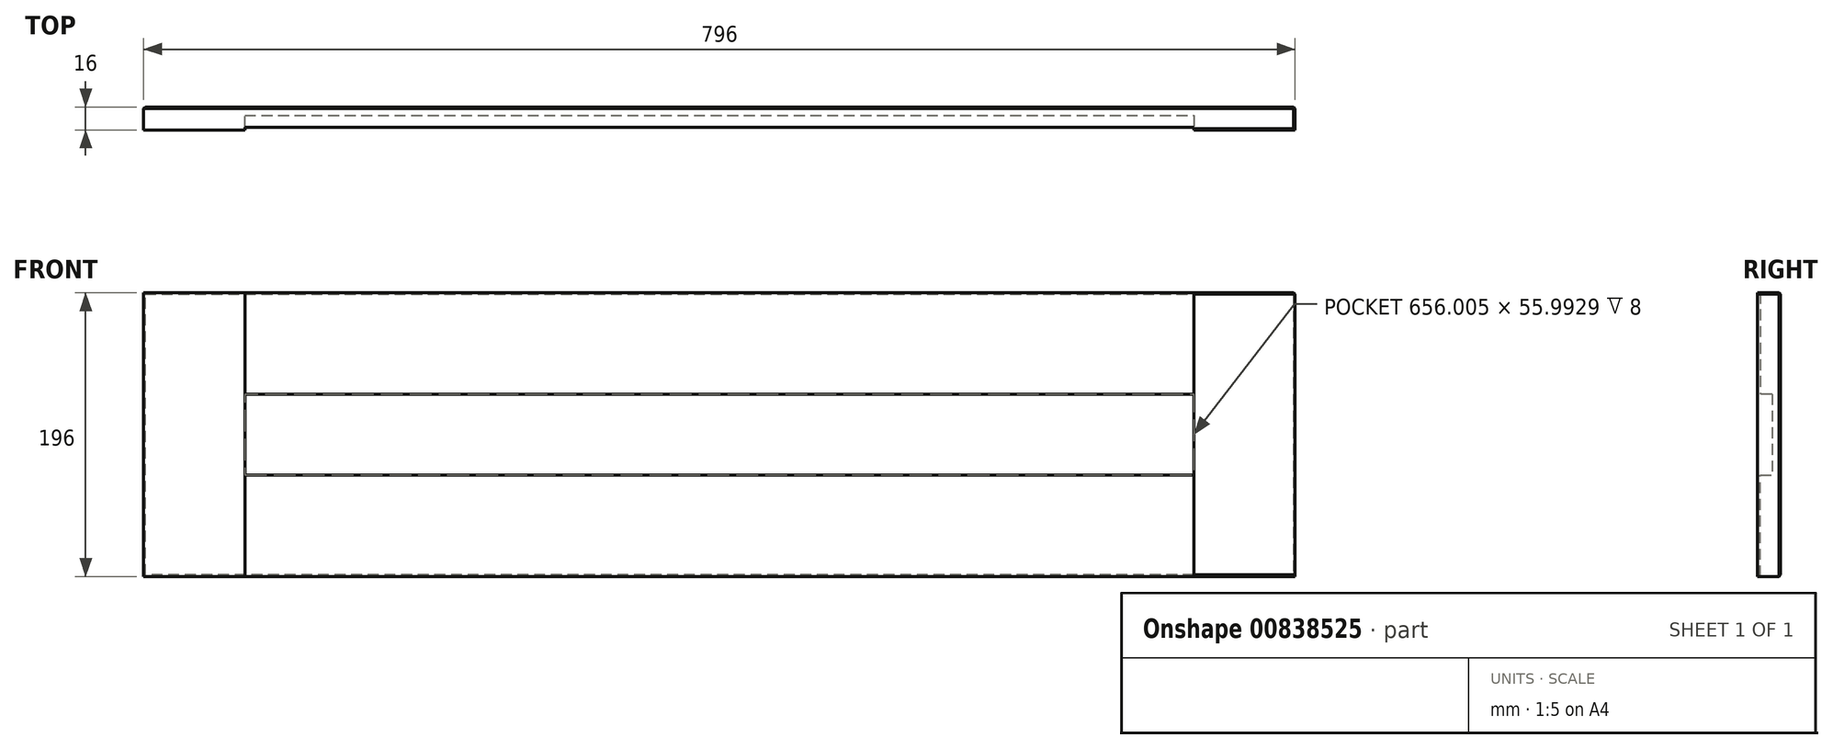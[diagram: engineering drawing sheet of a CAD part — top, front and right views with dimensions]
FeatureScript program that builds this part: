
annotation { "Feature Type Name" : "Feature", "Feature Type Description" : "" }
export const myFeature = defineFeature(function(context is Context, id is Id, definition is map)
    precondition{}
    {
        {
            var Q0;
            Q0=qCreatedBy(makeId("Front.planeOp"),FACE);
            var sketch = newSketch(context, id + "F0", { "sketchPlane" : qUnion([Q0])});
            skLineSegment(sketch, "E0.bottom", {"start": v(0, 0) * mm, "end": v(35.9, 0) * mm});
            skLineSegment(sketch, "E0.top", {"start": v(0, 30.12) * mm, "end": v(35.9, 30.12) * mm});
            skLineSegment(sketch, "E0.left", {"start": v(0, 0) * mm, "end": v(0, 30.12) * mm});
            skLineSegment(sketch, "E0.right", {"start": v(35.9, 0) * mm, "end": v(35.9, 30.12) * mm});
            skSolve(sketch);
        }
        {
            var Q0;
            Q0=makeQuery(id+"F0.imprint","IMPRINT",FACE,{"disambiguationData":[TD([[makeQuery(id+"F0.imprint","IMPRINT",EDGE,{"derivedFrom":sQuery(id+"F0.wireOp",EDGE,"E0.bottom")}),1.0]])]});
            extrude(context, id + "F1", {"entities" : qUnion([Q0]), "depth" : 16 * mm, "offsetDistance" : 25.4 * mm});
        }
        {
            var Q0;
            Q0=makeQuery(id+"F1.opExtrude","SWEPT_FACE",FACE,{"disambiguationData":[OSD([sQuery(id+"F0.wireOp",EDGE,"E0.left")])]});
            extrude(context, id + "F2", {"entities" : qUnion([Q0]), "operationType" : NewBodyOperationType.ADD, "oppositeDirection" : true, "depth" : 196 * mm, "offsetDistance" : 25 * mm});
        }
        {
            var Q0;
            {var subQ0=sQuery(id+"F0.wireOp",EDGE,"E0.bottom");Q0=makeQuery(id+"F2.boolean.opBoolean","MERGE",FACE,{"derivedFrom":[makeQuery(id+"F1.opExtrude","SWEPT_FACE",FACE,{"disambiguationData":[OSD([subQ0])]}),makeQuery(id+"F2.opExtrude","SWEPT_FACE",FACE,{"disambiguationData":[OSD([subQ0,sQuery(id+"F0.wireOp",EDGE,"E0.left")])]})]});}
            extrude(context, id + "F3", {"entities" : qUnion([Q0]), "operationType" : NewBodyOperationType.ADD, "oppositeDirection" : true, "depth" : 796 * mm, "offsetDistance" : 25 * mm});
        }
        {
            var Q0;
            {var subQ0=sQuery(id+"F0.wireOp",EDGE,"E0.left");var subQ1=sQuery(id+"F0.wireOp",EDGE,"E0.bottom");Q0=makeQuery(id+"F3.boolean.opBoolean","MERGE",FACE,{"derivedFrom":[makeQuery(id+"F2.boolean.opBoolean","MERGE",FACE,{"derivedFrom":[makeQuery(id+"F1.opExtrude","CAP_FACE",FACE,{"disambiguationData":[OSD([subQ1,sQuery(id+"F0.wireOp",EDGE,"E0.top"),subQ0,sQuery(id+"F0.wireOp",EDGE,"E0.right")])],"isStart":false}),makeQuery(id+"F2.opExtrude","SWEPT_FACE",FACE,{"disambiguationData":[OSD([subQ0]),TDD([makeQuery(id+"F1.opExtrude","CAP_EDGE",EDGE,{"disambiguationData":[OSD([subQ0])],"isStart":false})])]})]}),makeQuery(id+"F3.opExtrude","SWEPT_FACE",FACE,{"disambiguationData":[OSD([subQ1,subQ0]),TDD([makeQuery(id+"F2.boolean.opBoolean","MERGE",EDGE,{"derivedFrom":[makeQuery(id+"F1.opExtrude","CAP_EDGE",EDGE,{"disambiguationData":[OSD([subQ1])],"isStart":false}),makeQuery(id+"F2.opExtrude","SWEPT_EDGE",EDGE,{"disambiguationData":[OSD([subQ1,subQ0]),TDD([makeQuery(id+"F1.opExtrude","CAP_VERTEX",VERTEX,{"disambiguationData":[OSD([subQ1,subQ0])],"isStart":false})])]})]})])]})]});}
            var sketch = newSketch(context, id + "F4", { "sketchPlane" : qUnion([Q0])});
            skLineSegment(sketch, "E1.bottom", {"start": v(0, 796) * mm, "end": v(42.19, 796) * mm});
            skLineSegment(sketch, "E1.top", {"start": v(0, 751.57) * mm, "end": v(42.19, 751.57) * mm});
            skLineSegment(sketch, "E1.left", {"start": v(0, 796) * mm, "end": v(0, 751.57) * mm});
            skLineSegment(sketch, "E1.right", {"start": v(42.19, 796) * mm, "end": v(42.19, 751.57) * mm});
            skLineSegment(sketch, "E2.bottom", {"start": v(196, 796) * mm, "end": v(153.6, 796) * mm});
            skLineSegment(sketch, "E2.top", {"start": v(196, 746.75) * mm, "end": v(153.6, 746.75) * mm});
            skLineSegment(sketch, "E2.left", {"start": v(196, 796) * mm, "end": v(196, 746.75) * mm});
            skLineSegment(sketch, "E2.right", {"start": v(153.6, 796) * mm, "end": v(153.6, 746.75) * mm});
            skSolve(sketch);
        }
        {
            var Q0;
            Q0=makeQuery(id+"F4.imprint","IMPRINT",FACE,{"disambiguationData":[TD([[makeQuery(id+"F4.imprint","IMPRINT",EDGE,{"derivedFrom":sQuery(id+"F4.wireOp",EDGE,"E1.bottom")}),-1.0]])]});
            var Q1;
            Q1=makeQuery(id+"F4.imprint","IMPRINT",FACE,{"disambiguationData":[TD([[makeQuery(id+"F4.imprint","IMPRINT",EDGE,{"derivedFrom":sQuery(id+"F4.wireOp",EDGE,"E2.bottom")}),-1.0]])]});
            extrude(context, id + "F5", {"entities" : qUnion([Q0, Q1]), "operationType" : NewBodyOperationType.ADD, "depth" : 25 * mm, "offsetDistance" : 25 * mm});
        }
        {
            var Q0;
            {var subQ0=sQuery(id+"F0.wireOp",EDGE,"E0.left");var subQ1=sQuery(id+"F0.wireOp",EDGE,"E0.bottom");Q0=makeQuery(id+"F3.boolean.opBoolean","MERGE",FACE,{"derivedFrom":[makeQuery(id+"F2.boolean.opBoolean","MERGE",FACE,{"derivedFrom":[makeQuery(id+"F1.opExtrude","CAP_FACE",FACE,{"disambiguationData":[OSD([subQ1,sQuery(id+"F0.wireOp",EDGE,"E0.top"),subQ0,sQuery(id+"F0.wireOp",EDGE,"E0.right")])],"isStart":false}),makeQuery(id+"F2.opExtrude","SWEPT_FACE",FACE,{"disambiguationData":[OSD([subQ0]),TDD([makeQuery(id+"F1.opExtrude","CAP_EDGE",EDGE,{"disambiguationData":[OSD([subQ0])],"isStart":false})])]})]}),makeQuery(id+"F3.opExtrude","SWEPT_FACE",FACE,{"disambiguationData":[OSD([subQ1,subQ0]),TDD([makeQuery(id+"F2.boolean.opBoolean","MERGE",EDGE,{"derivedFrom":[makeQuery(id+"F1.opExtrude","CAP_EDGE",EDGE,{"disambiguationData":[OSD([subQ1])],"isStart":false}),makeQuery(id+"F2.opExtrude","SWEPT_EDGE",EDGE,{"disambiguationData":[OSD([subQ1,subQ0]),TDD([makeQuery(id+"F1.opExtrude","CAP_VERTEX",VERTEX,{"disambiguationData":[OSD([subQ1,subQ0])],"isStart":false})])]})]})])]})]});}
            var sketch = newSketch(context, id + "F6", { "sketchPlane" : qUnion([Q0])});
            skLineSegment(sketch, "E3.bottom", {"start": v(196, 0) * mm, "end": v(163.38, 0) * mm});
            skLineSegment(sketch, "E3.top", {"start": v(196, 46.55) * mm, "end": v(163.38, 46.55) * mm});
            skLineSegment(sketch, "E3.left", {"start": v(196, 0) * mm, "end": v(196, 46.55) * mm});
            skLineSegment(sketch, "E3.right", {"start": v(163.38, 0) * mm, "end": v(163.38, 46.55) * mm});
            skLineSegment(sketch, "E4.bottom", {"start": v(0, 0) * mm, "end": v(50.28, 0) * mm});
            skLineSegment(sketch, "E4.top", {"start": v(0, 44.4) * mm, "end": v(50.28, 44.4) * mm});
            skLineSegment(sketch, "E4.left", {"start": v(0, 0) * mm, "end": v(0, 44.4) * mm});
            skLineSegment(sketch, "E4.right", {"start": v(50.28, 0) * mm, "end": v(50.28, 44.4) * mm});
            skSolve(sketch);
        }
        {
            var Q0;
            Q0=makeQuery(id+"F6.imprint","IMPRINT",FACE,{"disambiguationData":[TD([[makeQuery(id+"F6.imprint","IMPRINT",EDGE,{"derivedFrom":sQuery(id+"F6.wireOp",EDGE,"E3.bottom")}),1.0]])]});
            var Q1;
            Q1=makeQuery(id+"F6.imprint","IMPRINT",FACE,{"disambiguationData":[TD([[makeQuery(id+"F6.imprint","IMPRINT",EDGE,{"derivedFrom":sQuery(id+"F6.wireOp",EDGE,"E4.bottom")}),1.0]])]});
            extrude(context, id + "F7", {"entities" : qUnion([Q0, Q1]), "operationType" : NewBodyOperationType.ADD, "depth" : 25 * mm, "offsetDistance" : 25 * mm});
        }
        {
            var Q0;
            Q0=makeQuery(id+"F7.opExtrude","SWEPT_FACE",FACE,{"disambiguationData":[OSD([sQuery(id+"F6.wireOp",EDGE,"E4.right")])]});
            extrude(context, id + "F8", {"entities" : qUnion([Q0]), "operationType" : NewBodyOperationType.ADD, "depth" : 19.72 * mm, "offsetDistance" : 25 * mm});
        }
        {
            var Q0;
            {var subQ0=sQuery(id+"F6.wireOp",EDGE,"E4.top");Q0=makeQuery(id+"F8.boolean.opBoolean","MERGE",FACE,{"derivedFrom":[makeQuery(id+"F7.opExtrude","SWEPT_FACE",FACE,{"disambiguationData":[OSD([subQ0])]}),makeQuery(id+"F8.opExtrude","SWEPT_FACE",FACE,{"disambiguationData":[OSD([subQ0,sQuery(id+"F6.wireOp",EDGE,"E4.right")])]})]});}
            extrude(context, id + "F9", {"entities" : qUnion([Q0]), "operationType" : NewBodyOperationType.ADD, "depth" : 25.6 * mm, "offsetDistance" : 25 * mm});
        }
        {
            var Q0;
            Q0=makeQuery(id+"F7.opExtrude","SWEPT_FACE",FACE,{"disambiguationData":[OSD([sQuery(id+"F6.wireOp",EDGE,"E3.right")])]});
            extrude(context, id + "F10", {"entities" : qUnion([Q0]), "operationType" : NewBodyOperationType.ADD, "depth" : 37.38 * mm, "offsetDistance" : 25 * mm});
        }
        {
            var Q0;
            {var subQ0=sQuery(id+"F6.wireOp",EDGE,"E3.top");Q0=makeQuery(id+"F10.boolean.opBoolean","MERGE",FACE,{"derivedFrom":[makeQuery(id+"F7.opExtrude","SWEPT_FACE",FACE,{"disambiguationData":[OSD([subQ0])]}),makeQuery(id+"F10.opExtrude","SWEPT_FACE",FACE,{"disambiguationData":[OSD([subQ0,sQuery(id+"F6.wireOp",EDGE,"E3.right")])]})]});}
            extrude(context, id + "F11", {"entities" : qUnion([Q0]), "operationType" : NewBodyOperationType.ADD, "depth" : 23.45 * mm, "offsetDistance" : 25 * mm});
        }
        {
            var Q0;
            Q0=makeQuery(id+"F5.opExtrude","SWEPT_FACE",FACE,{"disambiguationData":[OSD([sQuery(id+"F4.wireOp",EDGE,"E1.right")])]});
            extrude(context, id + "F12", {"entities" : qUnion([Q0]), "operationType" : NewBodyOperationType.ADD, "depth" : 27.8 * mm, "offsetDistance" : 25 * mm});
        }
        {
            var Q0;
            {var subQ0=sQuery(id+"F4.wireOp",EDGE,"E1.top");Q0=makeQuery(id+"F12.boolean.opBoolean","MERGE",FACE,{"derivedFrom":[makeQuery(id+"F5.opExtrude","SWEPT_FACE",FACE,{"disambiguationData":[OSD([subQ0])]}),makeQuery(id+"F12.opExtrude","SWEPT_FACE",FACE,{"disambiguationData":[OSD([subQ0,sQuery(id+"F4.wireOp",EDGE,"E1.right")])]})]});}
            extrude(context, id + "F13", {"entities" : qUnion([Q0]), "operationType" : NewBodyOperationType.ADD, "depth" : 25.57 * mm, "offsetDistance" : 25 * mm});
        }
        {
            var Q0;
            Q0=makeQuery(id+"F5.opExtrude","SWEPT_FACE",FACE,{"disambiguationData":[OSD([sQuery(id+"F4.wireOp",EDGE,"E2.top")])]});
            extrude(context, id + "F14", {"entities" : qUnion([Q0]), "operationType" : NewBodyOperationType.ADD, "depth" : 20.75 * mm, "offsetDistance" : 25 * mm});
        }
        {
            var Q0;
            {var subQ0=sQuery(id+"F4.wireOp",EDGE,"E2.right");Q0=makeQuery(id+"F14.boolean.opBoolean","MERGE",FACE,{"derivedFrom":[makeQuery(id+"F5.opExtrude","SWEPT_FACE",FACE,{"disambiguationData":[OSD([subQ0])]}),makeQuery(id+"F14.opExtrude","SWEPT_FACE",FACE,{"disambiguationData":[OSD([sQuery(id+"F4.wireOp",EDGE,"E2.top"),subQ0])]})]});}
            extrude(context, id + "F15", {"entities" : qUnion([Q0]), "operationType" : NewBodyOperationType.ADD, "depth" : 27.6 * mm, "offsetDistance" : 25 * mm});
        }
        {
            var Q0;
            {var subQ0=sQuery(id+"F0.wireOp",EDGE,"E0.left");var subQ1=sQuery(id+"F0.wireOp",EDGE,"E0.bottom");Q0=makeQuery(id+"F3.boolean.opBoolean","MERGE",FACE,{"derivedFrom":[makeQuery(id+"F2.boolean.opBoolean","MERGE",FACE,{"derivedFrom":[makeQuery(id+"F1.opExtrude","CAP_FACE",FACE,{"disambiguationData":[OSD([subQ1,sQuery(id+"F0.wireOp",EDGE,"E0.top"),subQ0,sQuery(id+"F0.wireOp",EDGE,"E0.right")])],"isStart":false}),makeQuery(id+"F2.opExtrude","SWEPT_FACE",FACE,{"disambiguationData":[OSD([subQ0]),TDD([makeQuery(id+"F1.opExtrude","CAP_EDGE",EDGE,{"disambiguationData":[OSD([subQ0])],"isStart":false})])]})]}),makeQuery(id+"F3.opExtrude","SWEPT_FACE",FACE,{"disambiguationData":[OSD([subQ1,subQ0]),TDD([makeQuery(id+"F2.boolean.opBoolean","MERGE",EDGE,{"derivedFrom":[makeQuery(id+"F1.opExtrude","CAP_EDGE",EDGE,{"disambiguationData":[OSD([subQ1])],"isStart":false}),makeQuery(id+"F2.opExtrude","SWEPT_EDGE",EDGE,{"disambiguationData":[OSD([subQ1,subQ0]),TDD([makeQuery(id+"F1.opExtrude","CAP_VERTEX",VERTEX,{"disambiguationData":[OSD([subQ1,subQ0])],"isStart":false})])]})]})])]})]});}
            var sketch = newSketch(context, id + "F16", { "sketchPlane" : qUnion([Q0])});
            skLineSegment(sketch, "E5.bottom", {"start": v(70, 726) * mm, "end": v(126, 726) * mm});
            skLineSegment(sketch, "E5.top", {"start": v(70, 70) * mm, "end": v(126, 70) * mm});
            skLineSegment(sketch, "E5.left", {"start": v(70, 726) * mm, "end": v(70, 70) * mm});
            skLineSegment(sketch, "E5.right", {"start": v(126, 726) * mm, "end": v(126, 70) * mm});
            skSolve(sketch);
        }
        {
            var Q0;
            Q0=makeQuery(id+"F16.imprint","IMPRINT",FACE,{"disambiguationData":[TD([[makeQuery(id+"F16.imprint","IMPRINT",EDGE,{"derivedFrom":sQuery(id+"F16.wireOp",EDGE,"E5.top")}),1.0]])]});
            extrude(context, id + "F17", {"entities" : qUnion([Q0]), "operationType" : NewBodyOperationType.REMOVE, "oppositeDirection" : true, "depth" : 10 * mm, "offsetDistance" : 25 * mm});
        }
        {
            var Q0;
            {var subQ2=sQuery(id+"F0.wireOp",EDGE,"E0.left");var subQ3=sQuery(id+"F0.wireOp",EDGE,"E0.bottom");var subQ4=makeQuery(id+"F1.opExtrude","CAP_FACE",FACE,{"disambiguationData":[OSD([subQ3,sQuery(id+"F0.wireOp",EDGE,"E0.top"),subQ2,sQuery(id+"F0.wireOp",EDGE,"E0.right")])],"isStart":false});var subQ7=makeQuery(id+"F3.opExtrude","SWEPT_FACE",FACE,{"disambiguationData":[OSD([subQ3,subQ2]),TDD([makeQuery(id+"F2.boolean.opBoolean","MERGE",EDGE,{"derivedFrom":[makeQuery(id+"F1.opExtrude","CAP_EDGE",EDGE,{"disambiguationData":[OSD([subQ3])],"isStart":false}),makeQuery(id+"F2.opExtrude","SWEPT_EDGE",EDGE,{"disambiguationData":[OSD([subQ3,subQ2]),TDD([makeQuery(id+"F1.opExtrude","CAP_VERTEX",VERTEX,{"disambiguationData":[OSD([subQ3,subQ2])],"isStart":false})])]})]})])]});var subQ8=makeQuery(id+"F2.opExtrude","SWEPT_FACE",FACE,{"disambiguationData":[OSD([subQ2]),TDD([makeQuery(id+"F1.opExtrude","CAP_EDGE",EDGE,{"disambiguationData":[OSD([subQ2])],"isStart":false})])]});Q0=makeQuery(id+"F17.boolean.opBoolean","SPLIT",FACE,{"disambiguationData":[TD([makeQuery(id+"F1.opExtrude","SWEPT_FACE",FACE,{"disambiguationData":[OSD([subQ3])]})])],"derivedFrom":makeQuery(id+"F3.boolean.opBoolean","MERGE",FACE,{"derivedFrom":[makeQuery(id+"F2.boolean.opBoolean","MERGE",FACE,{"derivedFrom":[subQ4,subQ8]}),subQ7]})});}
            var Q1;
            {var subQ2=sQuery(id+"F4.wireOp",EDGE,"E1.bottom");var subQ3=sQuery(id+"F0.wireOp",EDGE,"E0.left");var subQ4=sQuery(id+"F0.wireOp",EDGE,"E0.bottom");var subQ6=makeQuery(id+"F1.opExtrude","CAP_FACE",FACE,{"disambiguationData":[OSD([subQ4,sQuery(id+"F0.wireOp",EDGE,"E0.top"),subQ3,sQuery(id+"F0.wireOp",EDGE,"E0.right")])],"isStart":false});var subQ7=makeQuery(id+"F2.opExtrude","SWEPT_FACE",FACE,{"disambiguationData":[OSD([subQ3]),TDD([makeQuery(id+"F1.opExtrude","CAP_EDGE",EDGE,{"disambiguationData":[OSD([subQ3])],"isStart":false})])]});var subQ8=makeQuery(id+"F3.opExtrude","SWEPT_FACE",FACE,{"disambiguationData":[OSD([subQ4,subQ3]),TDD([makeQuery(id+"F2.boolean.opBoolean","MERGE",EDGE,{"derivedFrom":[makeQuery(id+"F1.opExtrude","CAP_EDGE",EDGE,{"disambiguationData":[OSD([subQ4])],"isStart":false}),makeQuery(id+"F2.opExtrude","SWEPT_EDGE",EDGE,{"disambiguationData":[OSD([subQ4,subQ3]),TDD([makeQuery(id+"F1.opExtrude","CAP_VERTEX",VERTEX,{"disambiguationData":[OSD([subQ4,subQ3])],"isStart":false})])]})]})])]});Q1=makeQuery(id+"F17.boolean.opBoolean","SPLIT",FACE,{"disambiguationData":[TD([makeQuery(id+"F5.opExtrude","SWEPT_FACE",FACE,{"disambiguationData":[OSD([subQ2])]})])],"derivedFrom":makeQuery(id+"F3.boolean.opBoolean","MERGE",FACE,{"derivedFrom":[makeQuery(id+"F2.boolean.opBoolean","MERGE",FACE,{"derivedFrom":[subQ6,subQ7]}),subQ8]})});}
            extrude(context, id + "F18", {"entities" : qUnion([Q0, Q1]), "operationType" : NewBodyOperationType.REMOVE, "oppositeDirection" : true, "depth" : 2 * mm, "offsetDistance" : 25 * mm});
        }
        {
            var Q0;
            {var subQ0=sQuery(id+"F4.wireOp",EDGE,"E1.right");var subQ1=sQuery(id+"F4.wireOp",EDGE,"E1.top");Q0=makeQuery(id+"F13.boolean.opBoolean","MERGE",FACE,{"derivedFrom":[makeQuery(id+"F12.boolean.opBoolean","MERGE",FACE,{"derivedFrom":[makeQuery(id+"F5.opExtrude","CAP_FACE",FACE,{"disambiguationData":[OSD([sQuery(id+"F4.wireOp",EDGE,"E1.bottom"),subQ1,sQuery(id+"F4.wireOp",EDGE,"E1.left"),subQ0])],"isStart":false}),makeQuery(id+"F12.opExtrude","SWEPT_FACE",FACE,{"disambiguationData":[OSD([subQ0]),TDD([makeQuery(id+"F5.opExtrude","CAP_EDGE",EDGE,{"disambiguationData":[OSD([subQ0])],"isStart":false})])]})]}),makeQuery(id+"F13.opExtrude","SWEPT_FACE",FACE,{"disambiguationData":[OSD([subQ1,subQ0]),TDD([makeQuery(id+"F12.boolean.opBoolean","MERGE",EDGE,{"derivedFrom":[makeQuery(id+"F5.opExtrude","CAP_EDGE",EDGE,{"disambiguationData":[OSD([subQ1])],"isStart":false}),makeQuery(id+"F12.opExtrude","SWEPT_EDGE",EDGE,{"disambiguationData":[OSD([subQ1,subQ0]),TDD([makeQuery(id+"F5.opExtrude","CAP_VERTEX",VERTEX,{"disambiguationData":[OSD([subQ1,subQ0])],"isStart":false})])]})]})])]})]});}
            var Q1;
            {var subQ0=sQuery(id+"F4.wireOp",EDGE,"E2.right");var subQ1=sQuery(id+"F4.wireOp",EDGE,"E2.top");Q1=makeQuery(id+"F15.boolean.opBoolean","MERGE",FACE,{"derivedFrom":[makeQuery(id+"F14.boolean.opBoolean","MERGE",FACE,{"derivedFrom":[makeQuery(id+"F5.opExtrude","CAP_FACE",FACE,{"disambiguationData":[OSD([sQuery(id+"F4.wireOp",EDGE,"E2.bottom"),subQ1,sQuery(id+"F4.wireOp",EDGE,"E2.left"),subQ0])],"isStart":false}),makeQuery(id+"F14.opExtrude","SWEPT_FACE",FACE,{"disambiguationData":[OSD([subQ1]),TDD([makeQuery(id+"F5.opExtrude","CAP_EDGE",EDGE,{"disambiguationData":[OSD([subQ1])],"isStart":false})])]})]}),makeQuery(id+"F15.opExtrude","SWEPT_FACE",FACE,{"disambiguationData":[OSD([subQ1,subQ0]),TDD([makeQuery(id+"F14.boolean.opBoolean","MERGE",EDGE,{"derivedFrom":[makeQuery(id+"F5.opExtrude","CAP_EDGE",EDGE,{"disambiguationData":[OSD([subQ0])],"isStart":false}),makeQuery(id+"F14.opExtrude","SWEPT_EDGE",EDGE,{"disambiguationData":[OSD([subQ1,subQ0]),TDD([makeQuery(id+"F5.opExtrude","CAP_VERTEX",VERTEX,{"disambiguationData":[OSD([subQ1,subQ0])],"isStart":false})])]})]})])]})]});}
            var Q2;
            {var subQ0=sQuery(id+"F6.wireOp",EDGE,"E4.right");var subQ1=sQuery(id+"F6.wireOp",EDGE,"E4.top");Q2=makeQuery(id+"F9.boolean.opBoolean","MERGE",FACE,{"derivedFrom":[makeQuery(id+"F8.boolean.opBoolean","MERGE",FACE,{"derivedFrom":[makeQuery(id+"F7.opExtrude","CAP_FACE",FACE,{"disambiguationData":[OSD([sQuery(id+"F6.wireOp",EDGE,"E4.bottom"),subQ1,sQuery(id+"F6.wireOp",EDGE,"E4.left"),subQ0])],"isStart":false}),makeQuery(id+"F8.opExtrude","SWEPT_FACE",FACE,{"disambiguationData":[OSD([subQ0]),TDD([makeQuery(id+"F7.opExtrude","CAP_EDGE",EDGE,{"disambiguationData":[OSD([subQ0])],"isStart":false})])]})]}),makeQuery(id+"F9.opExtrude","SWEPT_FACE",FACE,{"disambiguationData":[OSD([subQ1,subQ0]),TDD([makeQuery(id+"F8.boolean.opBoolean","MERGE",EDGE,{"derivedFrom":[makeQuery(id+"F7.opExtrude","CAP_EDGE",EDGE,{"disambiguationData":[OSD([subQ1])],"isStart":false}),makeQuery(id+"F8.opExtrude","SWEPT_EDGE",EDGE,{"disambiguationData":[OSD([subQ1,subQ0]),TDD([makeQuery(id+"F7.opExtrude","CAP_VERTEX",VERTEX,{"disambiguationData":[OSD([subQ1,subQ0])],"isStart":false})])]})]})])]})]});}
            var Q3;
            {var subQ0=sQuery(id+"F6.wireOp",EDGE,"E3.right");var subQ1=sQuery(id+"F6.wireOp",EDGE,"E3.top");Q3=makeQuery(id+"F11.boolean.opBoolean","MERGE",FACE,{"derivedFrom":[makeQuery(id+"F10.boolean.opBoolean","MERGE",FACE,{"derivedFrom":[makeQuery(id+"F7.opExtrude","CAP_FACE",FACE,{"disambiguationData":[OSD([sQuery(id+"F6.wireOp",EDGE,"E3.bottom"),subQ1,sQuery(id+"F6.wireOp",EDGE,"E3.left"),subQ0])],"isStart":false}),makeQuery(id+"F10.opExtrude","SWEPT_FACE",FACE,{"disambiguationData":[OSD([subQ0]),TDD([makeQuery(id+"F7.opExtrude","CAP_EDGE",EDGE,{"disambiguationData":[OSD([subQ0])],"isStart":false})])]})]}),makeQuery(id+"F11.opExtrude","SWEPT_FACE",FACE,{"disambiguationData":[OSD([subQ1,subQ0]),TDD([makeQuery(id+"F10.boolean.opBoolean","MERGE",EDGE,{"derivedFrom":[makeQuery(id+"F7.opExtrude","CAP_EDGE",EDGE,{"disambiguationData":[OSD([subQ1])],"isStart":false}),makeQuery(id+"F10.opExtrude","SWEPT_EDGE",EDGE,{"disambiguationData":[OSD([subQ1,subQ0]),TDD([makeQuery(id+"F7.opExtrude","CAP_VERTEX",VERTEX,{"disambiguationData":[OSD([subQ1,subQ0])],"isStart":false})])]})]})])]})]});}
            extrude(context, id + "F19", {"entities" : qUnion([Q0, Q1, Q2, Q3]), "operationType" : NewBodyOperationType.REMOVE, "oppositeDirection" : true, "depth" : 25 * mm, "offsetDistance" : 25 * mm});
        }
        {
            var Q0;
            {var subQ0=sQuery(id+"F4.wireOp",EDGE,"E2.left");var subQ1=sQuery(id+"F0.wireOp",EDGE,"E0.left");var subQ2=sQuery(id+"F0.wireOp",EDGE,"E0.bottom");var subQ3=sQuery(id+"F6.wireOp",EDGE,"E3.left");Q0=makeQuery(id+"F14.boolean.opBoolean","MERGE",FACE,{"derivedFrom":[makeQuery(id+"F11.boolean.opBoolean","MERGE",FACE,{"derivedFrom":[makeQuery(id+"F7.boolean.opBoolean","MERGE",FACE,{"derivedFrom":[makeQuery(id+"F5.boolean.opBoolean","MERGE",FACE,{"derivedFrom":[makeQuery(id+"F3.boolean.opBoolean","MERGE",FACE,{"derivedFrom":[makeQuery(id+"F2.opExtrude","CAP_FACE",FACE,{"disambiguationData":[OSD([subQ1])],"isStart":false}),makeQuery(id+"F3.opExtrude","SWEPT_FACE",FACE,{"disambiguationData":[OSD([subQ2,subQ1]),TDD([makeQuery(id+"F2.opExtrude","CAP_EDGE",EDGE,{"disambiguationData":[OSD([subQ2,subQ1])],"isStart":false})])]})]}),makeQuery(id+"F5.opExtrude","SWEPT_FACE",FACE,{"disambiguationData":[OSD([subQ0])]})]}),makeQuery(id+"F7.opExtrude","SWEPT_FACE",FACE,{"disambiguationData":[OSD([subQ3])]})]}),makeQuery(id+"F11.opExtrude","SWEPT_FACE",FACE,{"disambiguationData":[OSD([subQ2,subQ1,sQuery(id+"F6.wireOp",EDGE,"E3.top"),subQ3])]})]}),makeQuery(id+"F14.opExtrude","SWEPT_FACE",FACE,{"disambiguationData":[OSD([subQ2,subQ1,sQuery(id+"F4.wireOp",EDGE,"E2.top"),subQ0])]})]});}
            extrude(context, id + "F20", {"entities" : qUnion([Q0]), "operationType" : NewBodyOperationType.ADD, "depth" : 200 * mm, "offsetDistance" : 25 * mm});
        }
        {
            var Q0;
            {var subQ0=sQuery(id+"F4.wireOp",EDGE,"E2.right");var subQ1=sQuery(id+"F4.wireOp",EDGE,"E2.top");Q0=makeQuery(id+"F18.boolean.opBoolean","MERGE",FACE,{"derivedFrom":[makeQuery(id+"F15.opExtrude","CAP_FACE",FACE,{"disambiguationData":[OSD([subQ1,subQ0])],"isStart":false}),makeQuery(id+"F18.opExtrude","SWEPT_FACE",FACE,{"disambiguationData":[OSD([subQ1,subQ0])]})]});}
            var Q1;
            {var subQ0=sQuery(id+"F6.wireOp",EDGE,"E3.right");var subQ1=sQuery(id+"F6.wireOp",EDGE,"E3.top");Q1=makeQuery(id+"F18.boolean.opBoolean","MERGE",FACE,{"derivedFrom":[makeQuery(id+"F11.boolean.opBoolean","MERGE",FACE,{"derivedFrom":[makeQuery(id+"F10.opExtrude","CAP_FACE",FACE,{"disambiguationData":[OSD([subQ0])],"isStart":false}),makeQuery(id+"F11.opExtrude","SWEPT_FACE",FACE,{"disambiguationData":[OSD([subQ1,subQ0]),TDD([makeQuery(id+"F10.opExtrude","CAP_EDGE",EDGE,{"disambiguationData":[OSD([subQ1,subQ0])],"isStart":false})])]})]}),makeQuery(id+"F17.boolean.opBoolean","COPY",FACE,{"derivedFrom":makeQuery(id+"F17.opExtrude","SWEPT_FACE",FACE,{"disambiguationData":[OSD([sQuery(id+"F16.wireOp",EDGE,"E5.right")])]})}),makeQuery(id+"F18.opExtrude","SWEPT_FACE",FACE,{"disambiguationData":[OSD([subQ1,subQ0])]})]});}
            extrude(context, id + "F21", {"entities" : qUnion([Q0, Q1]), "operationType" : NewBodyOperationType.REMOVE, "oppositeDirection" : true, "depth" : 200 * mm, "offsetDistance" : 25 * mm});
        }
        {
            var Q0;
            Q0=makeQuery(id+"F17.boolean.opBoolean","COPY",FACE,{"derivedFrom":makeQuery(id+"F17.opExtrude","SWEPT_FACE",FACE,{"disambiguationData":[OSD([sQuery(id+"F16.wireOp",EDGE,"E5.bottom")])]})});
            var Q1;
            {var subQ0=sQuery(id+"F16.wireOp",EDGE,"E5.right");var subQ1=sQuery(id+"F16.wireOp",EDGE,"E5.bottom");var subQ2=sQuery(id+"F4.wireOp",EDGE,"E2.right");var subQ3=sQuery(id+"F4.wireOp",EDGE,"E2.top");var subQ4=makeQuery(id+"F17.boolean.opBoolean","COPY",EDGE,{"derivedFrom":makeQuery(id+"F17.opExtrude","SWEPT_EDGE",EDGE,{"disambiguationData":[OSD([subQ3,subQ2,subQ1,subQ0])]})});Q1=makeQuery(id+"F21.boolean.opBoolean","COPY",FACE,{"derivedFrom":makeQuery(id+"F21.opExtrude","SWEPT_FACE",FACE,{"disambiguationData":[OSD([subQ3,subQ2,subQ1,subQ0]),TDD([makeQuery(id+"F18.boolean.opBoolean","MERGE",EDGE,{"derivedFrom":[subQ4,makeQuery(id+"F18.opExtrude","SWEPT_EDGE",EDGE,{"disambiguationData":[OSD([subQ3,subQ2,subQ1,subQ0])]})]}),makeQuery(id+"F18.boolean.opBoolean","SPLIT",EDGE,{"derivedFrom":subQ4})])]})});}
            extrude(context, id + "F22", {"entities" : qUnion([Q0, Q1]), "operationType" : NewBodyOperationType.ADD, "depth" : 600 * mm, "offsetDistance" : 25 * mm});
        }
        {
            var Q0;
            {var subQ0=sQuery(id+"F4.wireOp",EDGE,"E2.bottom");var subQ1=sQuery(id+"F0.wireOp",EDGE,"E0.left");var subQ2=sQuery(id+"F0.wireOp",EDGE,"E0.bottom");var subQ3=sQuery(id+"F4.wireOp",EDGE,"E1.bottom");Q0=makeQuery(id+"F20.boolean.opBoolean","MERGE",FACE,{"derivedFrom":[makeQuery(id+"F15.boolean.opBoolean","MERGE",FACE,{"derivedFrom":[makeQuery(id+"F12.boolean.opBoolean","MERGE",FACE,{"derivedFrom":[makeQuery(id+"F5.boolean.opBoolean","MERGE",FACE,{"derivedFrom":[makeQuery(id+"F3.opExtrude","CAP_FACE",FACE,{"disambiguationData":[OSD([subQ2,subQ1])],"isStart":false}),makeQuery(id+"F5.opExtrude","SWEPT_FACE",FACE,{"disambiguationData":[OSD([subQ3])]}),makeQuery(id+"F5.opExtrude","SWEPT_FACE",FACE,{"disambiguationData":[OSD([subQ0])]})]}),makeQuery(id+"F12.opExtrude","SWEPT_FACE",FACE,{"disambiguationData":[OSD([subQ2,subQ1,subQ3,sQuery(id+"F4.wireOp",EDGE,"E1.right")])]})]}),makeQuery(id+"F15.opExtrude","SWEPT_FACE",FACE,{"disambiguationData":[OSD([subQ2,subQ1,subQ0,sQuery(id+"F4.wireOp",EDGE,"E2.right")])]})]}),makeQuery(id+"F20.opExtrude","SWEPT_FACE",FACE,{"disambiguationData":[OSD([subQ2,subQ1,subQ0,sQuery(id+"F4.wireOp",EDGE,"E2.left")])]})]});}
            extrude(context, id + "F23", {"entities" : qUnion([Q0]), "operationType" : NewBodyOperationType.REMOVE, "oppositeDirection" : true, "depth" : 600 * mm, "offsetDistance" : 25 * mm});
        }
        {
            var Q0;
            Q0=makeQuery(id+"F20.opExtrude","CAP_FACE",FACE,{"disambiguationData":[OSD([sQuery(id+"F0.wireOp",EDGE,"E0.bottom"),sQuery(id+"F0.wireOp",EDGE,"E0.left"),sQuery(id+"F4.wireOp",EDGE,"E2.top"),sQuery(id+"F4.wireOp",EDGE,"E2.left"),sQuery(id+"F6.wireOp",EDGE,"E3.top"),sQuery(id+"F6.wireOp",EDGE,"E3.left")])],"isStart":false});
            extrude(context, id + "F24", {"entities" : qUnion([Q0]), "operationType" : NewBodyOperationType.ADD, "depth" : 400 * mm, "offsetDistance" : 25 * mm});
        }
        {
            var Q0;
            Q0=makeQuery(id+"F21.boolean.opBoolean","COPY",FACE,{"derivedFrom":makeQuery(id+"F21.opExtrude","CAP_FACE",FACE,{"disambiguationData":[OSD([sQuery(id+"F6.wireOp",EDGE,"E3.top"),sQuery(id+"F6.wireOp",EDGE,"E3.right"),sQuery(id+"F16.wireOp",EDGE,"E5.right")])],"isStart":false})});
            extrude(context, id + "F25", {"entities" : qUnion([Q0]), "operationType" : NewBodyOperationType.REMOVE, "oppositeDirection" : true, "depth" : 400 * mm, "offsetDistance" : 25 * mm});
        }
        {
            var Q0;
            {var subQ0=sQuery(id+"F4.wireOp",EDGE,"E1.right");var subQ1=sQuery(id+"F4.wireOp",EDGE,"E1.bottom");var subQ2=sQuery(id+"F0.wireOp",EDGE,"E0.left");var subQ3=sQuery(id+"F0.wireOp",EDGE,"E0.bottom");Q0=makeQuery(id+"F23.boolean.opBoolean","COPY",EDGE,{"derivedFrom":makeQuery(id+"F23.opExtrude","CAP_EDGE",EDGE,{"disambiguationData":[OSD([subQ3,subQ2,subQ1,subQ0]),TDD([makeQuery(id+"F19.boolean.opBoolean","COPY",EDGE,{"derivedFrom":makeQuery(id+"F19.opExtrude","CAP_EDGE",EDGE,{"disambiguationData":[OSD([subQ3,subQ2,subQ1,subQ0])],"isStart":false})})])],"isStart":false})});}
            var Q1;
            {var subQ0=sQuery(id+"F0.wireOp",EDGE,"E0.left");var subQ1=sQuery(id+"F0.wireOp",EDGE,"E0.bottom");Q1=makeQuery(id+"F19.boolean.opBoolean","MERGE",EDGE,{"derivedFrom":[makeQuery(id+"F3.boolean.opBoolean","MERGE",EDGE,{"derivedFrom":[makeQuery(id+"F1.opExtrude","CAP_EDGE",EDGE,{"disambiguationData":[OSD([subQ0])],"isStart":false}),makeQuery(id+"F3.opExtrude","SWEPT_EDGE",EDGE,{"disambiguationData":[OSD([subQ1,subQ0]),TDD([makeQuery(id+"F1.opExtrude","CAP_VERTEX",VERTEX,{"disambiguationData":[OSD([subQ1,subQ0])],"isStart":false})])]})]}),makeQuery(id+"F19.opExtrude","CAP_EDGE",EDGE,{"disambiguationData":[OSD([subQ1,subQ0,sQuery(id+"F6.wireOp",EDGE,"E4.top"),sQuery(id+"F6.wireOp",EDGE,"E4.left")])],"isStart":false}),makeQuery(id+"F19.opExtrude","CAP_EDGE",EDGE,{"disambiguationData":[OSD([subQ1,subQ0,sQuery(id+"F4.wireOp",EDGE,"E1.top"),sQuery(id+"F4.wireOp",EDGE,"E1.left")])],"isStart":false})]});}
            var Q2;
            Q2=makeQuery(id+"F19.boolean.opBoolean","COPY",EDGE,{"derivedFrom":makeQuery(id+"F19.opExtrude","CAP_EDGE",EDGE,{"disambiguationData":[OSD([sQuery(id+"F0.wireOp",EDGE,"E0.bottom"),sQuery(id+"F0.wireOp",EDGE,"E0.left"),sQuery(id+"F6.wireOp",EDGE,"E4.bottom"),sQuery(id+"F6.wireOp",EDGE,"E4.right")])],"isStart":false})});
            var Q3;
            Q3=makeQuery(id+"F24.opExtrude","CAP_EDGE",EDGE,{"disambiguationData":[OSD([sQuery(id+"F0.wireOp",EDGE,"E0.bottom"),sQuery(id+"F0.wireOp",EDGE,"E0.left"),sQuery(id+"F4.wireOp",EDGE,"E2.top"),sQuery(id+"F4.wireOp",EDGE,"E2.left"),sQuery(id+"F6.wireOp",EDGE,"E3.top"),sQuery(id+"F6.wireOp",EDGE,"E3.left")])],"isStart":false});
            var Q4;
            {var subQ0=sQuery(id+"F4.wireOp",EDGE,"E2.left");var subQ1=sQuery(id+"F4.wireOp",EDGE,"E2.bottom");Q4=makeQuery(id+"F24.boolean.opBoolean","MERGE",EDGE,{"derivedFrom":[makeQuery(id+"F23.boolean.opBoolean","COPY",EDGE,{"derivedFrom":makeQuery(id+"F23.opExtrude","CAP_EDGE",EDGE,{"disambiguationData":[OSD([sQuery(id+"F0.wireOp",EDGE,"E0.bottom"),sQuery(id+"F0.wireOp",EDGE,"E0.left"),subQ1,subQ0,sQuery(id+"F4.wireOp",EDGE,"E2.right")])],"isStart":false})}),makeQuery(id+"F24.opExtrude","SWEPT_EDGE",EDGE,{"disambiguationData":[OSD([subQ1,subQ0])]})]});}
            var Q5;
            {var subQ0=sQuery(id+"F6.wireOp",EDGE,"E3.left");var subQ1=sQuery(id+"F6.wireOp",EDGE,"E3.bottom");Q5=makeQuery(id+"F24.boolean.opBoolean","MERGE",EDGE,{"derivedFrom":[makeQuery(id+"F20.boolean.opBoolean","MERGE",EDGE,{"derivedFrom":[makeQuery(id+"F19.boolean.opBoolean","COPY",EDGE,{"derivedFrom":makeQuery(id+"F19.opExtrude","CAP_EDGE",EDGE,{"disambiguationData":[OSD([sQuery(id+"F0.wireOp",EDGE,"E0.bottom"),sQuery(id+"F0.wireOp",EDGE,"E0.left"),subQ1,sQuery(id+"F6.wireOp",EDGE,"E3.right")])],"isStart":false})}),makeQuery(id+"F20.opExtrude","SWEPT_EDGE",EDGE,{"disambiguationData":[OSD([subQ1,subQ0])]})]}),makeQuery(id+"F24.opExtrude","SWEPT_EDGE",EDGE,{"disambiguationData":[OSD([subQ1,subQ0])]})]});}
            var Q6;
            {var subQ0=sQuery(id+"F0.wireOp",EDGE,"E0.left");var subQ1=sQuery(id+"F0.wireOp",EDGE,"E0.bottom");Q6=makeQuery(id+"F24.boolean.opBoolean","MERGE",FACE,{"derivedFrom":[makeQuery(id+"F20.boolean.opBoolean","MERGE",FACE,{"derivedFrom":[makeQuery(id+"F3.boolean.opBoolean","MERGE",FACE,{"derivedFrom":[makeQuery(id+"F2.boolean.opBoolean","MERGE",FACE,{"derivedFrom":[makeQuery(id+"F1.opExtrude","CAP_FACE",FACE,{"disambiguationData":[OSD([subQ1,sQuery(id+"F0.wireOp",EDGE,"E0.top"),subQ0,sQuery(id+"F0.wireOp",EDGE,"E0.right")])],"isStart":true}),makeQuery(id+"F2.opExtrude","SWEPT_FACE",FACE,{"disambiguationData":[OSD([subQ0]),TDD([makeQuery(id+"F1.opExtrude","CAP_EDGE",EDGE,{"disambiguationData":[OSD([subQ0])],"isStart":true})])]})]}),makeQuery(id+"F3.opExtrude","SWEPT_FACE",FACE,{"disambiguationData":[OSD([subQ1,subQ0]),TDD([makeQuery(id+"F2.boolean.opBoolean","MERGE",EDGE,{"derivedFrom":[makeQuery(id+"F1.opExtrude","CAP_EDGE",EDGE,{"disambiguationData":[OSD([subQ1])],"isStart":true}),makeQuery(id+"F2.opExtrude","SWEPT_EDGE",EDGE,{"disambiguationData":[OSD([subQ1,subQ0]),TDD([makeQuery(id+"F1.opExtrude","CAP_VERTEX",VERTEX,{"disambiguationData":[OSD([subQ1,subQ0])],"isStart":true})])]})]})])]})]}),makeQuery(id+"F20.opExtrude","SWEPT_FACE",FACE,{"disambiguationData":[OSD([subQ1,subQ0])]})]}),makeQuery(id+"F24.opExtrude","SWEPT_FACE",FACE,{"disambiguationData":[OSD([subQ1,subQ0])]})]});}
            chamfer(context, id + "F26", {"entities" : qUnion([Q0, Q1, Q2, Q3, Q4, Q5, Q6]), "width" : 1 * mm, "tangentPropagation" : true});
        }
    });
